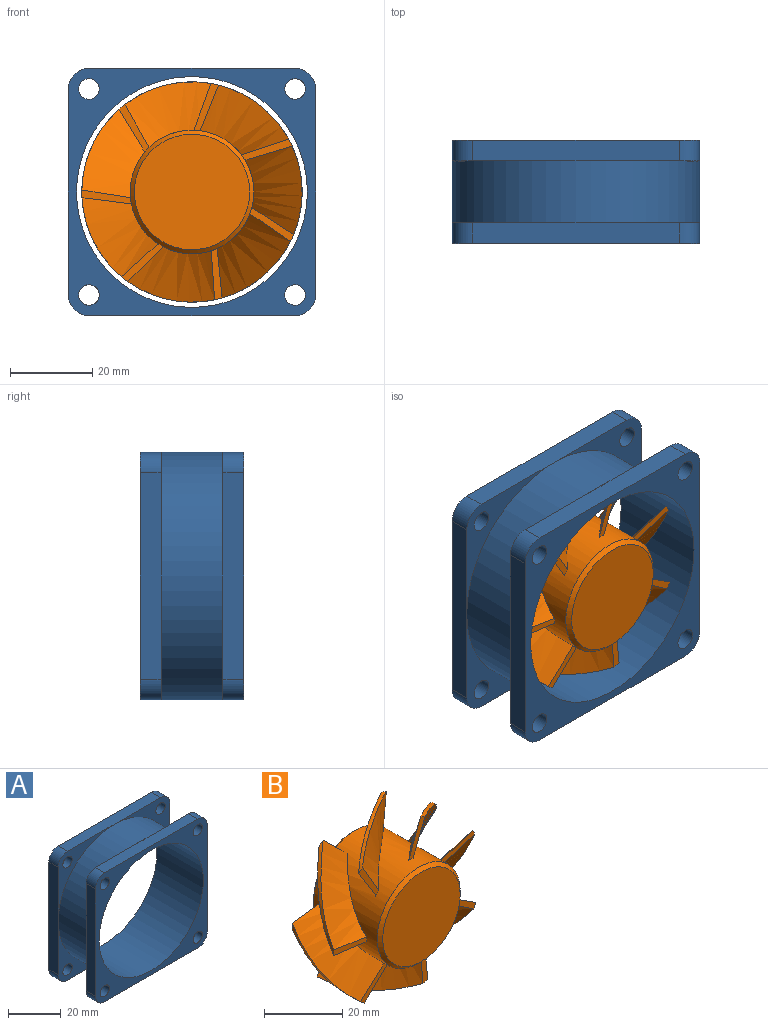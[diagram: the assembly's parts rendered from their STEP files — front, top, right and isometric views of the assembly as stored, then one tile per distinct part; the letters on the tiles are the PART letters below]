
ASSEMBLY  parts=2 mates=1
PART A: 36 faces, bbox 60x25x60 mm
  f0: plane 30x30mm, normal (0,-1,0), area 168.1mm2, adj f5,f23,f24,f25,f34
  f1: plane 30x30mm, normal (0,-1,0), area 168.1mm2, adj f5,f23,f29,f30,f35
  f2: plane 30x30mm, normal (0,-1,0), area 168.1mm2, adj f23,f27,f28,f29,f32
  f3: plane 30x30mm, normal (0,-1,0), area 168.1mm2, adj f23,f25,f26,f27,f33
  f4: plane 50x5mm, normal (1,0,0), area 250mm2, adj f6,f9,f10,f11,f12
  f5: plane 50x5mm, normal (1,0,0), area 250mm2, adj f0,f1,f24,f30,f31
  f6: plane 30x30mm, normal (0,1,0), area 168.1mm2, adj f4,f12,f13,f20,f23
  f7: plane 30x30mm, normal (0,1,0), area 168.1mm2, adj f13,f14,f15,f19,f23
  f8: plane 30x30mm, normal (0,1,0), area 168.1mm2, adj f15,f16,f17,f22,f23
  f9: plane 60x60mm, normal (0,-1,0), area 1037mm2, adj f4,f11,f12,f13,f14,f15,f16,f17
  f10: plane 30x30mm, normal (0,1,0), area 168.1mm2, adj f4,f11,f17,f21,f23
  f11: cylinder r=5mm len=5mm, axis (0,1,0), area 39.3mm2, adj f4,f9,f10,f17
  f12: cylinder r=5mm len=5mm, axis (0,1,0), area 39.3mm2, adj f4,f6,f9,f13
  f13: plane 50x5mm, normal (0,0,1), area 250mm2, adj f6,f7,f9,f12,f14
  f14: cylinder r=5mm len=5mm, axis (0,1,0), area 39.3mm2, adj f7,f9,f13,f15
  f15: plane 50x5mm, normal (-1,0,0), area 250mm2, adj f7,f8,f9,f14,f16
  f16: cylinder r=5mm len=5mm, axis (0,1,0), area 39.3mm2, adj f8,f9,f15,f17
  f17: plane 50x5mm, normal (0,0,-1), area 250mm2, adj f8,f9,f10,f11,f16
  f18: cylinder r=28mm len=56mm, axis (0,1,0), area 4398.2mm2, adj f9,f31
  f19: cylinder r=2.5mm len=5mm, axis (0,1,0), area 78.5mm2, adj f7,f9
  f20: cylinder r=2.5mm len=5mm, axis (0,1,0), area 78.5mm2, adj f6,f9
  f21: cylinder r=2.5mm len=5mm, axis (0,1,0), area 78.5mm2, adj f9,f10
  f22: cylinder r=2.5mm len=5mm, axis (0,1,0), area 78.5mm2, adj f8,f9
  f23: cylinder r=30mm len=60mm, axis (0,1,0), area 2827.4mm2, adj f0,f1,f2,f3,f6,f7,f8,f10
  f24: cylinder r=5mm len=5mm, axis (0,-1,0), area 39.3mm2, adj f0,f5,f25,f31
  f25: plane 50x5mm, normal (0,0,-1), area 250mm2, adj f0,f3,f24,f26,f31
  f26: cylinder r=5mm len=5mm, axis (0,-1,0), area 39.3mm2, adj f3,f25,f27,f31
  f27: plane 50x5mm, normal (-1,0,0), area 250mm2, adj f2,f3,f26,f28,f31
  f28: cylinder r=5mm len=5mm, axis (0,-1,0), area 39.3mm2, adj f2,f27,f29,f31
  f29: plane 50x5mm, normal (0,0,1), area 250mm2, adj f1,f2,f28,f30,f31
  f30: cylinder r=5mm len=5mm, axis (0,-1,0), area 39.3mm2, adj f1,f5,f29,f31
  f31: plane 60x60mm, normal (0,1,0), area 1037mm2, adj f5,f18,f24,f25,f26,f27,f28,f29
  f32: cylinder r=2.5mm len=5mm, axis (0,-1,0), area 78.5mm2, adj f2,f31
  f33: cylinder r=2.5mm len=5mm, axis (0,-1,0), area 78.5mm2, adj f3,f31
  f34: cylinder r=2.5mm len=5mm, axis (0,-1,0), area 78.5mm2, adj f0,f31
  f35: cylinder r=2.5mm len=5mm, axis (0,-1,0), area 78.5mm2, adj f1,f31
PART B: 40 faces, bbox 60.1x25x65.2 mm
  f0: plane 28x28mm, normal (0,-1,0), area 615.8mm2, adj f2
  f1: plane 28x28mm, normal (0,1,0), area 615.8mm2, adj f3
  f2: cone r=14mm half-angle=45deg, axis (0,1,0), area 128.8mm2, adj f0,f28
  f3: cone r=14mm half-angle=45deg, axis (0,-1,0), area 128.8mm2, adj f1,f28
  f4: bspline ~30x27.89mm, area 307.1mm2, adj f5,f6,f28,f39
  f5: bspline ~30x11.16mm, area 19.8mm2, adj f4,f7,f28,f39
  f6: plane 12.29x5.1mm, normal (0,-1,0), area 19.9mm2, adj f4,f7,f28,f39
  f7: bspline ~30x27.89mm, area 307.1mm2, adj f5,f6,f28,f39
  f8: bspline ~25.9x24.55mm, area 307.1mm2, adj f9,f11,f28,f38
  f9: bspline ~12.07x8.26mm, area 19.8mm2, adj f8,f10,f28,f38
  f10: bspline ~25.53x24.85mm, area 307.1mm2, adj f9,f11,f28,f38
  f11: plane 11.47x5.97mm, normal (0,-1,0), area 19.9mm2, adj f8,f10,f28,f38
  f12: bspline ~31.73x4.2mm, area 19.8mm2, adj f13,f14,f28,f37
  f13: bspline ~33.23x27.19mm, area 307.1mm2, adj f12,f15,f28,f37
  f14: bspline ~33.44x27.19mm, area 307.1mm2, adj f12,f15,f28,f37
  f15: plane 11.5x7.33mm, normal (0,-1,0), area 19.9mm2, adj f13,f14,f28,f37
  f16: bspline ~25.65x22.35mm, area 307.1mm2, adj f17,f19,f28,f36
  f17: bspline ~23.61x23.07mm, area 19.8mm2, adj f16,f18,f28,f36
  f18: bspline ~25.23x22.55mm, area 307.1mm2, adj f17,f19,f28,f36
  f19: plane 12.02x3.38mm, normal (0,-1,0), area 19.9mm2, adj f16,f18,f28,f36
  f20: bspline ~13.52x3.38mm, area 19.8mm2, adj f21,f22,f28,f35
  f21: bspline ~25.65x22.35mm, area 307.1mm2, adj f20,f23,f28,f35
  f22: bspline ~25.23x22.55mm, area 307.1mm2, adj f20,f23,f28,f35
  f23: plane 10.13x9.19mm, normal (0,-1,0), area 19.9mm2, adj f21,f22,f28,f35
  f24: bspline ~33.23x27.19mm, area 307.1mm2, adj f25,f27,f28,f34
  f25: bspline ~27.49x17.55mm, area 19.8mm2, adj f24,f26,f28,f34
  f26: bspline ~33.44x27.19mm, area 307.1mm2, adj f25,f27,f28,f34
  f27: plane 12.46x2.61mm, normal (0,-1,0), area 19.9mm2, adj f24,f26,f28,f34
  f28: cylinder r=15mm len=30mm, axis (0,1,0), area 1998.3mm2, adj f2,f3,f4,f5,f6,f7,f8,f9
  f29: plane 10.6x8.26mm, normal (0,-1,0), area 19.9mm2, adj f28,f30,f32,f33
  f30: bspline ~25.9x24.55mm, area 307.1mm2, adj f28,f29,f31,f33
  f31: bspline ~13.12x5.97mm, area 19.8mm2, adj f28,f30,f32,f33
  f32: bspline ~25.53x24.85mm, area 307.1mm2, adj f28,f29,f31,f33
  f33: cylinder r=26.73mm len=20.05mm, axis (0,1,0), area 29.3mm2, adj f29,f30,f31,f32
  f34: cylinder r=26.73mm len=25mm, axis (0,1,0), area 29.3mm2, adj f24,f25,f26,f27
  f35: cylinder r=26.73mm len=23.1mm, axis (0,1,0), area 29.3mm2, adj f20,f21,f22,f23
  f36: cylinder r=26.73mm len=23.1mm, axis (0,1,0), area 29.3mm2, adj f16,f17,f18,f19
  f37: cylinder r=26.73mm len=25mm, axis (0,1,0), area 29.3mm2, adj f12,f13,f14,f15
  f38: cylinder r=26.73mm len=20.05mm, axis (0,1,0), area 29.3mm2, adj f8,f9,f10,f11
  f39: cylinder r=26.73mm len=25.64mm, axis (0,1,0), area 29.3mm2, adj f4,f5,f6,f7
PLACE A at identity
PLACE B at identity fixed
MATE fastened A.f18 <-> B.f2  axis (0,1,0) through (30,20,30)mm
